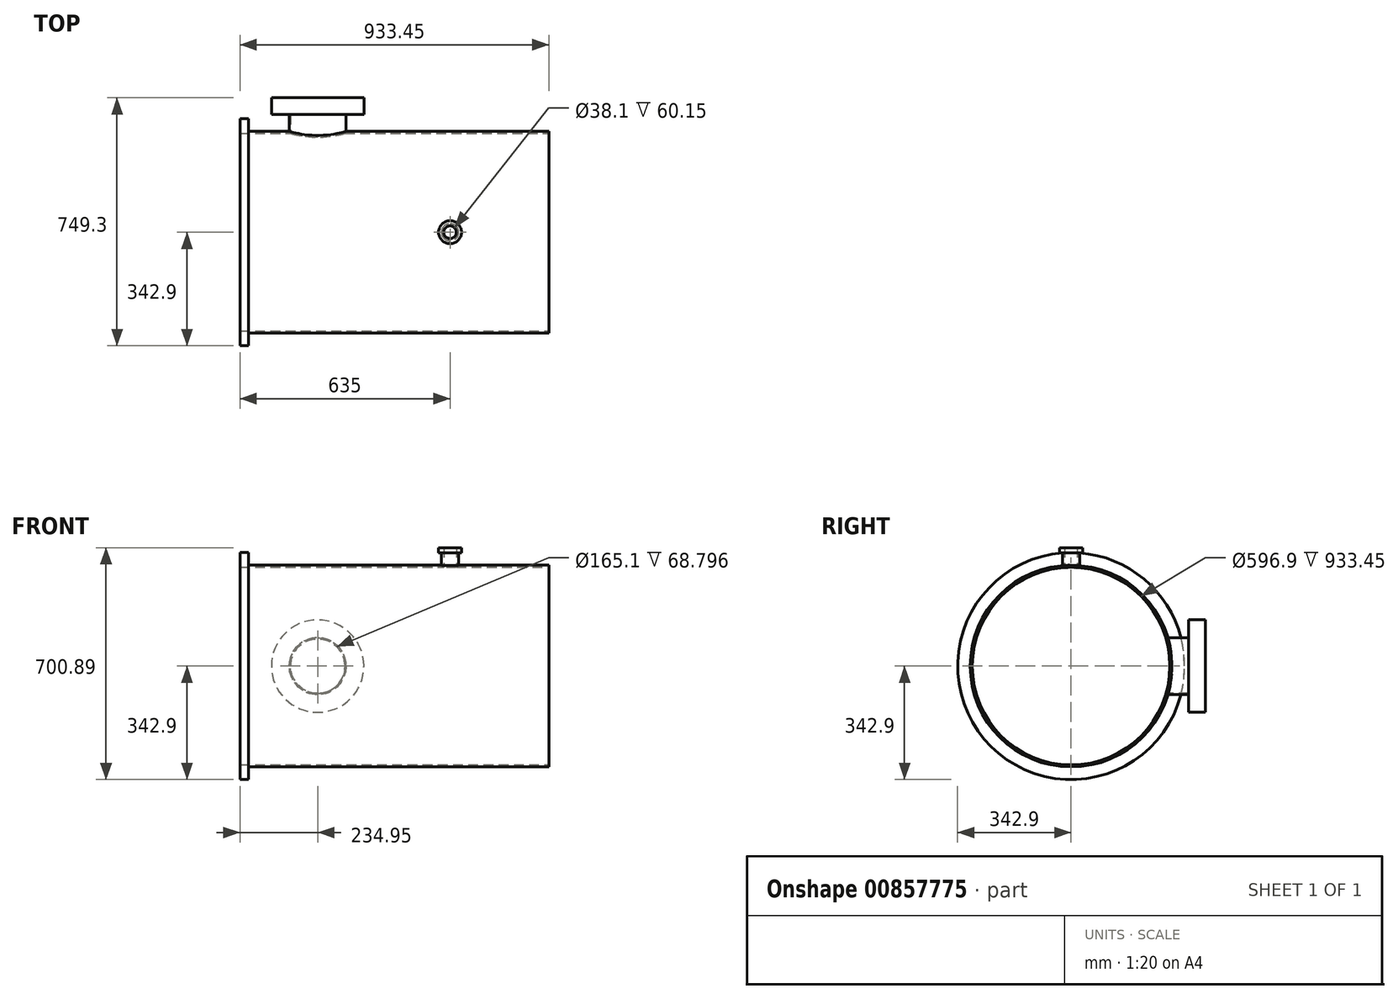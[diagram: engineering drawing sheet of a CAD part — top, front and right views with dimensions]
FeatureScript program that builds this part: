
annotation { "Feature Type Name" : "Feature", "Feature Type Description" : "" }
export const myFeature = defineFeature(function(context is Context, id is Id, definition is map)
    precondition{}
    {
        {
            var Q0;
            Q0=qCreatedBy(makeId("Right.planeOp"),FACE);
            var sketch = newSketch(context, id + "F0", { "sketchPlane" : qUnion([Q0])});
            skCircle(sketch, "E0", {"center": v(0, 0) * mm, "radius": 22.32 * mm});
            skSolve(sketch);
        }
        {
            var Q0;
            Q0=qCreatedBy(makeId("Top.planeOp"),FACE);
            var sketch = newSketch(context, id + "F1", { "sketchPlane" : qUnion([Q0])});
            skLineSegment(sketch, "E1.bottom", {"start": v(-457.2, 298.45) * mm, "end": v(450.85, 298.45) * mm});
            skLineSegment(sketch, "E1.top", {"start": v(-457.2, 304.8) * mm, "end": v(450.85, 304.8) * mm});
            skLineSegment(sketch, "E1.left", {"start": v(-457.2, 298.45) * mm, "end": v(-457.2, 304.8) * mm});
            skLineSegment(sketch, "E1.right", {"start": v(450.85, 298.45) * mm, "end": v(450.85, 304.8) * mm});
            skLineSegment(sketch, "E2.bottom", {"start": v(450.85, 298.45) * mm, "end": v(-459.4, 298.45) * mm});
            skLineSegment(sketch, "E2.top", {"start": v(450.85, 0) * mm, "end": v(-459.4, 0) * mm});
            skLineSegment(sketch, "E2.left", {"start": v(450.85, 298.45) * mm, "end": v(450.85, 0) * mm});
            skLineSegment(sketch, "E2.right", {"start": v(-459.4, 298.45) * mm, "end": v(-459.4, 0) * mm});
            skSolve(sketch);
        }
        {
            var Q0;
            Q0=makeQuery(id+"F1.imprint","IMPRINT",FACE,{"disambiguationData":[TD([[makeQuery(id+"F1.imprint","IMPRINT",EDGE,{"derivedFrom":sQuery(id+"F1.wireOp",EDGE,"E1.top")}),-1.0]])]});
            var Q1;
            Q1=sQuery(id+"F0.wireOp",EDGE,"E0");
            sweep(context, id + "F2", {"profiles" : qUnion([Q0]), "path" : qUnion([Q1])});
        }
        {
            var Q0;
            Q0=qCreatedBy(makeId("Front.planeOp"),FACE);
            var sketch = newSketch(context, id + "F3", { "sketchPlane" : qUnion([Q0])});
            skLineSegment(sketch, "E3", {"start": v(0, 0) * mm, "end": v(457.2, 0) * mm});
            skLineSegment(sketch, "E4", {"start": v(457.2, 0) * mm, "end": v(0, 0) * mm, "construction": true});
            skLineSegment(sketch, "E5", {"start": v(0, 304.8) * mm, "end": v(0, 0) * mm, "construction": true});
            skLineSegment(sketch, "E6", {"start": v(0, 304.8) * mm, "end": v(152.4, 304.8) * mm, "construction": true});
            skLineSegment(sketch, "E7", {"start": v(152.4, 304.8) * mm, "end": v(152.4, 0) * mm, "construction": true});
            skLineSegment(sketch, "E8", {"start": v(457.2, 0) * mm, "end": v(457.2, 302.42) * mm, "construction": true});
            skLineSegment(sketch, "E9", {"start": v(152.4, 304.8) * mm, "end": v(457.2, 302.42) * mm, "construction": true});
            skLineSegment(sketch, "E10.bottom", {"start": v(171.45, 304.65) * mm, "end": v(178.45, 304.65) * mm});
            skLineSegment(sketch, "E10.top", {"start": v(171.45, 342.75) * mm, "end": v(178.45, 342.75) * mm});
            skLineSegment(sketch, "E10.left", {"start": v(171.45, 304.65) * mm, "end": v(171.45, 342.75) * mm});
            skLineSegment(sketch, "E10.right", {"start": v(178.45, 304.65) * mm, "end": v(178.45, 342.75) * mm});
            skLineSegment(sketch, "E11", {"start": v(171.45, 342.75) * mm, "end": v(171.45, 358) * mm});
            skLineSegment(sketch, "E12", {"start": v(171.45, 358) * mm, "end": v(186.94, 358) * mm});
            skLineSegment(sketch, "E13", {"start": v(186.94, 358) * mm, "end": v(186.94, 342.75) * mm});
            skLineSegment(sketch, "E14", {"start": v(186.94, 342.75) * mm, "end": v(178.45, 342.75) * mm});
            skLineSegment(sketch, "E15", {"start": v(152.4, 304.8) * mm, "end": v(152.4, 406.43) * mm, "construction": true});
            skLineSegment(sketch, "E16.bottom", {"start": v(171.45, 315.57) * mm, "end": v(152.4, 315.57) * mm});
            skLineSegment(sketch, "E16.top", {"start": v(171.45, 281.7) * mm, "end": v(152.4, 281.7) * mm});
            skLineSegment(sketch, "E16.left", {"start": v(171.45, 315.57) * mm, "end": v(171.45, 281.7) * mm});
            skLineSegment(sketch, "E16.right", {"start": v(152.4, 315.57) * mm, "end": v(152.4, 281.7) * mm});
            skSolve(sketch);
        }
        {
            var Q0;
            Q0=makeQuery(id+"F3.imprint","IMPRINT",FACE,{"disambiguationData":[TD([[makeQuery(id+"F3.imprint","IMPRINT",EDGE,{"derivedFrom":sQuery(id+"F3.wireOp",EDGE,"E10.top")}),1.0]])]});
            var Q1;
            Q1=makeQuery(id+"F3.imprint","IMPRINT",FACE,{"disambiguationData":[TD([[makeQuery(id+"F3.imprint","IMPRINT",EDGE,{"derivedFrom":sQuery(id+"F3.wireOp",EDGE,"E10.bottom")}),1.0]])]});
            var Q2;
            Q2=sQuery(id+"F3.wireOp",EDGE,"E15");
            revolve(context, id + "F4", {"operationType" : NewBodyOperationType.ADD, "entities" : qUnion([Q0, Q1]), "axis" : qUnion([Q2]), "revolveType" : RevolveType.FULL});
        }
        {
            var Q0;
            Q0=makeQuery(id+"F2.opSweep","SWEPT_FACE",FACE,{"disambiguationData":[OSD([sQuery(id+"F0.wireOp",EDGE,"E0"),sQuery(id+"F1.wireOp",EDGE,"E1.left")])]});
            var sketch = newSketch(context, id + "F5", { "sketchPlane" : qUnion([Q0])});
            skCircle(sketch, "E17", {"center": v(0, 0) * mm, "radius": 342.9 * mm});
            skSolve(sketch);
        }
        {
            var Q0;
            Q0=makeQuery(id+"F5.imprint","IMPRINT",FACE,{"disambiguationData":[TD([[makeQuery(id+"F5.imprint","IMPRINT",EDGE,{"derivedFrom":sQuery(id+"F5.wireOp",EDGE,"E17")}),1.0]])]});
            var Q1;
            {var subQ0=sQuery(id+"F1.wireOp",EDGE,"E1.left");var subQ1=sQuery(id+"F0.wireOp",EDGE,"E0");Q1=makeQuery(id+"F5.imprint","IMPRINT",FACE,{"disambiguationData":[TD([[makeQuery(id+"F5.imprint","IMPRINT",EDGE,{"derivedFrom":makeQuery(id+"F2.opSweep","SWEPT_EDGE",EDGE,{"disambiguationData":[OSD([subQ1,sQuery(id+"F1.wireOp",EDGE,"E1.bottom"),subQ0])]})}),1.0]])]});}
            extrude(context, id + "F6", {"entities" : qUnion([Q0, Q1]), "operationType" : NewBodyOperationType.ADD, "depth" : 25.4 * mm});
        }
        {
            var Q0;
            Q0=qCreatedBy(makeId("Front.planeOp"),FACE);
            var sketch = newSketch(context, id + "F7", { "sketchPlane" : qUnion([Q0])});
            skLineSegment(sketch, "E18", {"start": v(0, 0) * mm, "end": v(-482.6, 0) * mm, "construction": true});
            skPoint(sketch, "E19", {"position": v(-247.65, 0) * mm});
            skCircle(sketch, "E20", {"center": v(-247.65, 0) * mm, "radius": 82.55 * mm});
            skCircle(sketch, "E21", {"center": v(-247.65, 0) * mm, "radius": 139.7 * mm});
            skCircle(sketch, "E22", {"center": v(-247.65, 0) * mm, "radius": 85.73 * mm});
            skSolve(sketch);
        }
        {
            var Q0;
            Q0=makeQuery(id+"F7.imprint","IMPRINT",FACE,{"disambiguationData":[TD([[makeQuery(id+"F7.imprint","IMPRINT",EDGE,{"derivedFrom":sQuery(id+"F7.wireOp",EDGE,"E20")}),1.0]])]});
            extrude(context, id + "F8", {"entities" : qUnion([Q0]), "operationType" : NewBodyOperationType.REMOVE, "oppositeDirection" : true, "depth" : 508 * mm});
        }
        {
            var Q0;
            Q0=makeQuery(id+"F7.imprint","IMPRINT",FACE,{"disambiguationData":[TD([[makeQuery(id+"F7.imprint","IMPRINT",EDGE,{"derivedFrom":sQuery(id+"F7.wireOp",EDGE,"E20")}),-1.0]])]});
            extrude(context, id + "F9", {"entities" : qUnion([Q0]), "operationType" : NewBodyOperationType.ADD, "oppositeDirection" : true, "depth" : 355.6 * mm, "hasSecondDirection" : true, "secondDirectionOppositeDirection" : true, "secondDirectionDepth" : 285.75 * mm});
        }
        {
            var Q0;
            Q0=makeQuery(id+"F7.imprint","IMPRINT",FACE,{"disambiguationData":[TD([[makeQuery(id+"F7.imprint","IMPRINT",EDGE,{"derivedFrom":sQuery(id+"F7.wireOp",EDGE,"E21")}),1.0]])]});
            var Q1;
            Q1=makeQuery(id+"F7.imprint","IMPRINT",FACE,{"disambiguationData":[TD([[makeQuery(id+"F7.imprint","IMPRINT",EDGE,{"derivedFrom":sQuery(id+"F7.wireOp",EDGE,"E20")}),-1.0]])]});
            var Q2;
            Q2=makeQuery(id+"F7.imprint","IMPRINT",FACE,{"disambiguationData":[TD([[makeQuery(id+"F7.imprint","IMPRINT",EDGE,{"derivedFrom":sQuery(id+"F7.wireOp",EDGE,"E20")}),1.0]])]});
            extrude(context, id + "F10", {"entities" : qUnion([Q0, Q1, Q2]), "operationType" : NewBodyOperationType.ADD, "oppositeDirection" : true, "depth" : 406.4 * mm, "hasSecondDirection" : true, "secondDirectionOppositeDirection" : true, "secondDirectionDepth" : 355.6 * mm});
        }
        {
            var Q0;
            Q0=makeQuery(id+"F1.imprint","IMPRINT",FACE,{"disambiguationData":[TD([[makeQuery(id+"F1.imprint","IMPRINT",EDGE,{"derivedFrom":sQuery(id+"F1.wireOp",EDGE,"E2.top")}),-1.0]])]});
            var Q1;
            Q1=sQuery(id+"F1.wireOp",EDGE,"E2.top");
            revolve(context, id + "F11", {"entities" : qUnion([Q0]), "axis" : qUnion([Q1]), "revolveType" : RevolveType.FULL});
        }
        {
            var Q0;
            Q0=makeQuery(id+"F11.opRevolve","SWEPT_BODY",BODY,{"disambiguationData":[OSD([sQuery(id+"F1.wireOp",EDGE,"E2.bottom"),sQuery(id+"F1.wireOp",EDGE,"E2.top"),sQuery(id+"F1.wireOp",EDGE,"E2.left"),sQuery(id+"F1.wireOp",EDGE,"E2.right")])]});
            var Q1;
            Q1=makeQuery(id+"F2.opSweep","SWEPT_BODY",BODY,{"disambiguationData":[OSD([sQuery(id+"F0.wireOp",EDGE,"E0"),sQuery(id+"F1.wireOp",EDGE,"E1.top"),sQuery(id+"F1.wireOp",EDGE,"E1.left"),sQuery(id+"F1.wireOp",EDGE,"E1.right"),sQuery(id+"F1.wireOp",EDGE,"E2.bottom")])]});
            booleanBodies(context, id + "F12", {"operationType" : BooleanOperationType.SUBTRACTION, "tools" : qUnion([Q0]), "targets" : qUnion([Q1])});
        }
        {
            var Q0;
            {var subQ3=sQuery(id+"F3.wireOp",EDGE,"E16.bottom");Q0=makeQuery(id+"F3.imprint","IMPRINT",FACE,{"disambiguationData":[TD([[makeQuery(id+"F3.imprint","IMPRINT",EDGE,{"derivedFrom":subQ3}),1.0]])]});}
            var Q1;
            Q1=sQuery(id+"F3.wireOp",EDGE,"E15");
            revolve(context, id + "F13", {"operationType" : NewBodyOperationType.REMOVE, "entities" : qUnion([Q0]), "axis" : qUnion([Q1]), "revolveType" : RevolveType.FULL, "oppositeDirection" : true});
        }
    });
